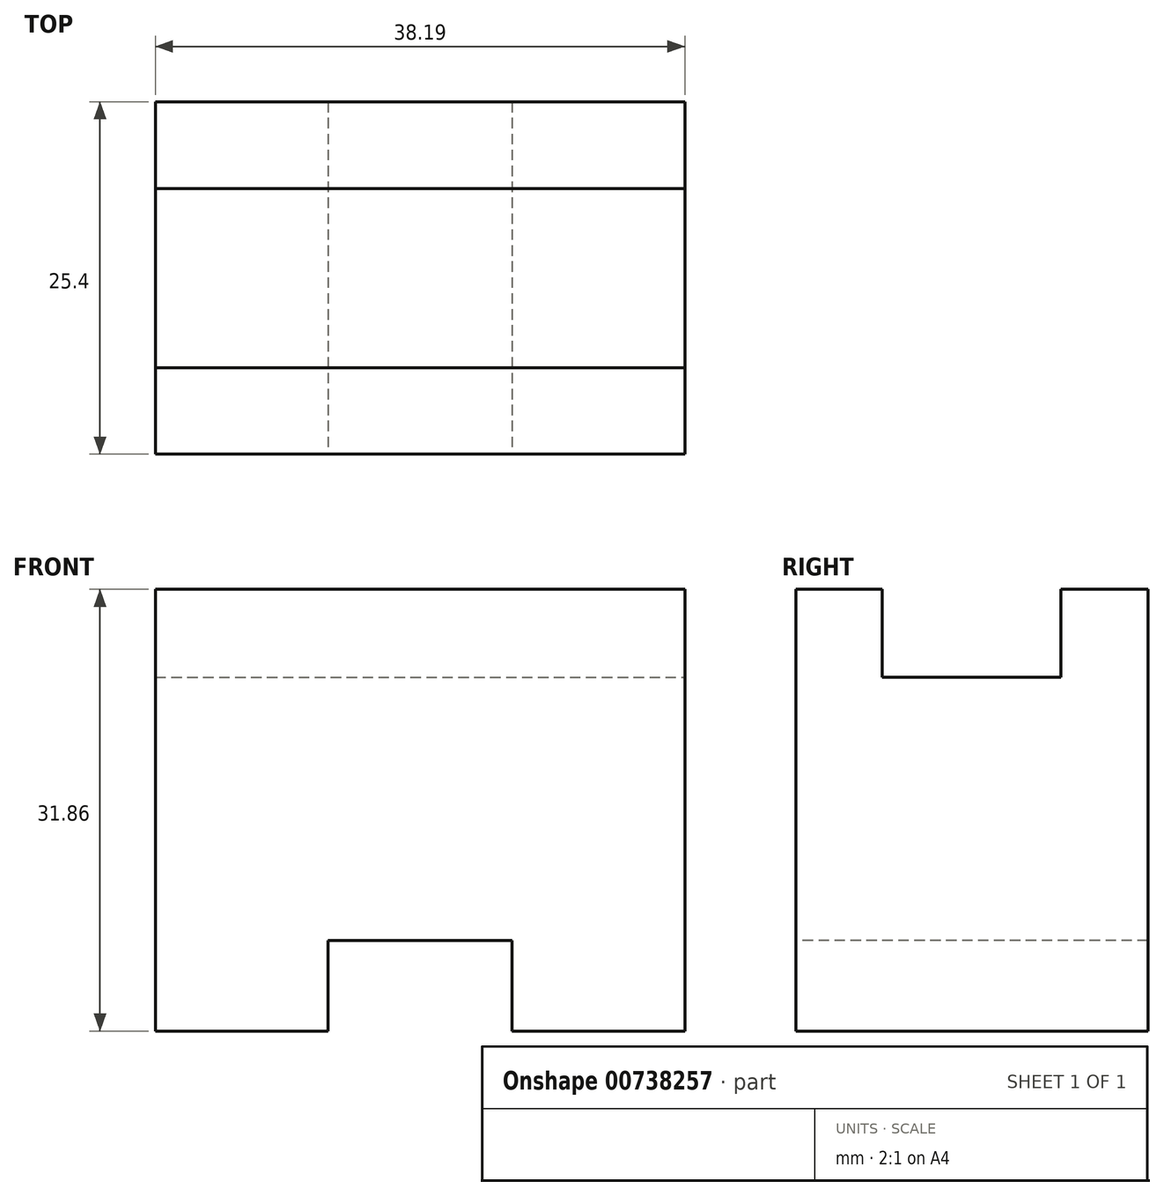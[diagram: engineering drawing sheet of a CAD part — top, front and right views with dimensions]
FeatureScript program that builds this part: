
annotation { "Feature Type Name" : "Feature", "Feature Type Description" : "" }
export const myFeature = defineFeature(function(context is Context, id is Id, definition is map)
    precondition{}
    {
        {
            var Q0;
            Q0=qCreatedBy(makeId("Front.planeOp"),FACE);
            var sketch = newSketch(context, id + "F0", { "sketchPlane" : qUnion([Q0])});
            skLineSegment(sketch, "E0", {"start": v(-6.94, 0) * mm, "end": v(-45.13, 0) * mm});
            skLineSegment(sketch, "E1", {"start": v(-6.94, 0) * mm, "end": v(-6.94, 31.86) * mm});
            skLineSegment(sketch, "E2", {"start": v(-6.94, 31.86) * mm, "end": v(-45.13, 31.86) * mm});
            skLineSegment(sketch, "E3", {"start": v(-45.13, 31.86) * mm, "end": v(-45.13, 0) * mm});
            skSolve(sketch);
        }
        {
            var Q0;
            Q0 = qSketchRegion(id + "F0", true);
            extrude(context, id + "F1", {"entities" : qUnion([Q0]), "depth" : 25.4 * mm, "offsetDistance" : 25.4 * mm});
        }
        {
            var Q0;
            Q0=makeQuery(id+"F1.opExtrude","SWEPT_FACE",FACE,{"disambiguationData":[OSD([sQuery(id+"F0.wireOp",EDGE,"E2")])]});
            var sketch = newSketch(context, id + "F2", { "sketchPlane" : qUnion([Q0])});
            skLineSegment(sketch, "E4", {"start": v(-45.13, -19.16) * mm, "end": v(-6.94, -19.16) * mm});
            skLineSegment(sketch, "E5", {"start": v(-45.13, -6.26) * mm, "end": v(-6.94, -6.26) * mm});
            skSolve(sketch);
        }
        {
            var Q0;
            {var subQ0=sQuery(id+"F2.wireOp",EDGE,"E4");Q0=makeQuery(id+"F2.imprint","IMPRINT",FACE,{"disambiguationData":[TD([[makeQuery(id+"F2.imprint","IMPRINT",EDGE,{"derivedFrom":subQ0}),1.0]])]});}
            extrude(context, id + "F3", {"entities" : qUnion([Q0]), "operationType" : NewBodyOperationType.REMOVE, "oppositeDirection" : true, "depth" : 6.35 * mm, "offsetDistance" : 25.4 * mm});
        }
        {
            var Q0;
            Q0=makeQuery(id+"F1.opExtrude","CAP_FACE",FACE,{"disambiguationData":[OSD([sQuery(id+"F0.wireOp",EDGE,"E0"),sQuery(id+"F0.wireOp",EDGE,"E1"),sQuery(id+"F0.wireOp",EDGE,"E2"),sQuery(id+"F0.wireOp",EDGE,"E3")])],"isStart":false});
            var sketch = newSketch(context, id + "F4", { "sketchPlane" : qUnion([Q0])});
            skLineSegment(sketch, "E6", {"start": v(-32.67, 0) * mm, "end": v(-32.67, 6.53) * mm});
            skLineSegment(sketch, "E7", {"start": v(-32.67, 6.53) * mm, "end": v(-19.4, 6.53) * mm});
            skLineSegment(sketch, "E8", {"start": v(-19.4, 6.53) * mm, "end": v(-19.4, 0) * mm});
            skSolve(sketch);
        }
        {
            var Q0;
            {var subQ0=sQuery(id+"F4.wireOp",EDGE,"E6");Q0=makeQuery(id+"F4.imprint","IMPRINT",FACE,{"disambiguationData":[TD([[makeQuery(id+"F4.imprint","IMPRINT",EDGE,{"derivedFrom":subQ0}),-1.0]])]});}
            extrude(context, id + "F5", {"entities" : qUnion([Q0]), "operationType" : NewBodyOperationType.REMOVE, "endBound" : BoundingType.THROUGH_ALL, "oppositeDirection" : true, "depth" : 25.4 * mm, "offsetDistance" : 25.4 * mm});
        }
    });
